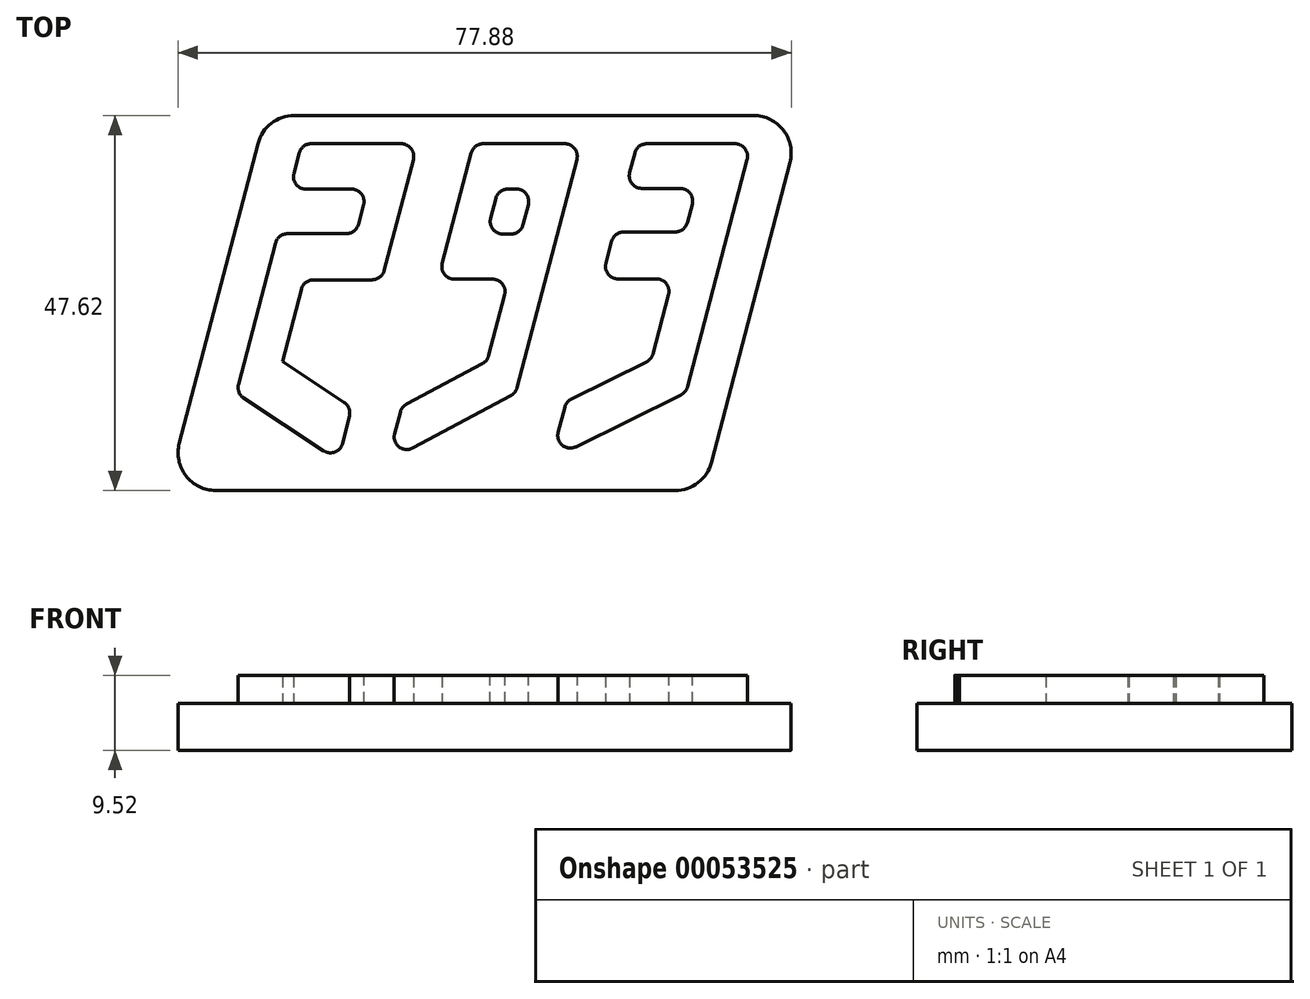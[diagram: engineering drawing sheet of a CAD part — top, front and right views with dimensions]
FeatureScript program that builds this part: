
annotation { "Feature Type Name" : "Feature", "Feature Type Description" : "" }
export const myFeature = defineFeature(function(context is Context, id is Id, definition is map)
    precondition{}
    {
        {
            var Q0;
            Q0=qCreatedBy(makeId("Top.planeOp"),FACE);
            var sketch = newSketch(context, id + "F0", { "sketchPlane" : qUnion([Q0])});
            skLineSegment(sketch, "E0", {"start": v(0, 0) * mm, "end": v(18.18, 0) * mm});
            skLineSegment(sketch, "E1", {"start": v(0, 0) * mm, "end": v(-6.01, -22.93) * mm});
            skLineSegment(sketch, "E2", {"start": v(-6.01, -22.93) * mm, "end": v(5.94, -22.93) * mm});
            skLineSegment(sketch, "E3", {"start": v(5.94, -22.93) * mm, "end": v(2.3, -36.8) * mm});
            skLineSegment(sketch, "E4", {"start": v(2.3, -36.8) * mm, "end": v(-12.18, -44.54) * mm});
            skLineSegment(sketch, "E5", {"start": v(-12.18, -44.54) * mm, "end": v(-14.61, -53.83) * mm});
            skLineSegment(sketch, "E6", {"start": v(-14.61, -53.83) * mm, "end": v(7.12, -42.22) * mm});
            skLineSegment(sketch, "E7", {"start": v(7.12, -42.22) * mm, "end": v(18.18, 0) * mm});
            skLineSegment(sketch, "E8", {"start": v(4.18, -7.66) * mm, "end": v(9.95, -7.66) * mm});
            skLineSegment(sketch, "E9", {"start": v(9.95, -7.66) * mm, "end": v(7.94, -15.3) * mm});
            skLineSegment(sketch, "E10", {"start": v(7.94, -15.3) * mm, "end": v(2.18, -15.3) * mm});
            skLineSegment(sketch, "E11", {"start": v(2.18, -15.3) * mm, "end": v(4.18, -7.66) * mm});
            skLineSegment(sketch, "E12", {"start": v(27.7, 0) * mm, "end": v(47, 0) * mm});
            skLineSegment(sketch, "E13", {"start": v(47, 0) * mm, "end": v(35.97, -42.12) * mm});
            skLineSegment(sketch, "E14", {"start": v(35.97, -42.12) * mm, "end": v(13.14, -53.38) * mm});
            skLineSegment(sketch, "E15", {"start": v(13.14, -53.38) * mm, "end": v(15.68, -43.68) * mm});
            skLineSegment(sketch, "E16", {"start": v(15.68, -43.68) * mm, "end": v(30.12, -36.55) * mm});
            skLineSegment(sketch, "E17", {"start": v(30.12, -36.55) * mm, "end": v(33.7, -22.9) * mm});
            skLineSegment(sketch, "E18", {"start": v(33.7, -22.9) * mm, "end": v(21.7, -22.9) * mm});
            skLineSegment(sketch, "E19", {"start": v(21.7, -22.9) * mm, "end": v(23.8, -14.93) * mm});
            skLineSegment(sketch, "E20", {"start": v(23.8, -14.93) * mm, "end": v(35.78, -14.93) * mm});
            skLineSegment(sketch, "E21", {"start": v(35.78, -14.93) * mm, "end": v(37.72, -7.56) * mm});
            skLineSegment(sketch, "E22", {"start": v(37.72, -7.56) * mm, "end": v(25.73, -7.56) * mm});
            skLineSegment(sketch, "E23", {"start": v(25.73, -7.56) * mm, "end": v(27.7, 0) * mm});
            skLineSegment(sketch, "E24", {"start": v(-29.14, 0) * mm, "end": v(-9.52, 0) * mm});
            skLineSegment(sketch, "E25", {"start": v(-9.52, 0) * mm, "end": v(-15.56, -23.05) * mm});
            skLineSegment(sketch, "E26", {"start": v(-29.14, 0) * mm, "end": v(-31.15, -7.69) * mm});
            skLineSegment(sketch, "E27", {"start": v(-31.15, -7.69) * mm, "end": v(-17.95, -7.69) * mm});
            skLineSegment(sketch, "E28", {"start": v(-17.95, -7.69) * mm, "end": v(-19.92, -15.23) * mm});
            skLineSegment(sketch, "E29", {"start": v(-19.92, -15.23) * mm, "end": v(-33.13, -15.23) * mm});
            skLineSegment(sketch, "E30", {"start": v(-15.56, -23.05) * mm, "end": v(-28.77, -23.05) * mm});
            skLineSegment(sketch, "E31", {"start": v(-28.77, -23.05) * mm, "end": v(-32.4, -36.9) * mm});
            skLineSegment(sketch, "E32", {"start": v(-32.4, -36.9) * mm, "end": v(-20.7, -44.63) * mm});
            skLineSegment(sketch, "E33", {"start": v(-20.7, -44.63) * mm, "end": v(-22.88, -53.67) * mm});
            skLineSegment(sketch, "E34", {"start": v(-22.88, -53.67) * mm, "end": v(-40.2, -42.23) * mm});
            skLineSegment(sketch, "E35", {"start": v(-40.2, -42.23) * mm, "end": v(-33.13, -15.23) * mm});
            skLineSegment(sketch, "E36", {"start": v(-36.54, 0.04) * mm, "end": v(-49.85, -50.76) * mm});
            skLineSegment(sketch, "E37", {"start": v(-43.7, -58.72) * mm, "end": v(34.12, -58.72) * mm});
            skLineSegment(sketch, "E38", {"start": v(40.26, -53.98) * mm, "end": v(53.58, -3.18) * mm});
            skLineSegment(sketch, "E39", {"start": v(-30.4, 4.78) * mm, "end": v(47.43, 4.78) * mm});
            skPoint(sketch, "E40.visualSharp", {"position": v(-35.3, 4.78) * mm});
            skArc(sketch, "E40.filletArc", {"start": v(-30.4, 4.78) * mm, "mid": v(-34.27, 3.45) * mm, "end": v(-36.54, 0.04) * mm});
            skPoint(sketch, "E41.visualSharp", {"position": v(-51.94, -58.72) * mm});
            skArc(sketch, "E41.filletArc", {"start": v(-49.85, -50.76) * mm, "mid": v(-48.73, -56.25) * mm, "end": v(-43.7, -58.72) * mm});
            skPoint(sketch, "E42.visualSharp", {"position": v(39.02, -58.72) * mm});
            skArc(sketch, "E42.filletArc", {"start": v(34.12, -58.72) * mm, "mid": v(38, -57.4) * mm, "end": v(40.26, -53.98) * mm});
            skPoint(sketch, "E43.visualSharp", {"position": v(55.66, 4.78) * mm});
            skArc(sketch, "E43.filletArc", {"start": v(53.58, -3.18) * mm, "mid": v(52.46, 2.3) * mm, "end": v(47.43, 4.78) * mm});
            skSolve(sketch);
        }
        {
            var Q0;
            Q0=makeQuery(id+"F0.imprint","IMPRINT",FACE,{"disambiguationData":[TD([[makeQuery(id+"F0.imprint","IMPRINT",EDGE,{"derivedFrom":sQuery(id+"F0.wireOp",EDGE,"E12")}),-1.0]])]});
            var Q1;
            Q1=makeQuery(id+"F0.imprint","IMPRINT",FACE,{"disambiguationData":[TD([[makeQuery(id+"F0.imprint","IMPRINT",EDGE,{"derivedFrom":sQuery(id+"F0.wireOp",EDGE,"E0")}),-1.0]])]});
            var Q2;
            Q2=makeQuery(id+"F0.imprint","IMPRINT",FACE,{"disambiguationData":[TD([[makeQuery(id+"F0.imprint","IMPRINT",EDGE,{"derivedFrom":sQuery(id+"F0.wireOp",EDGE,"E24")}),-1.0]])]});
            extrude(context, id + "F1", {"entities" : qUnion([Q0, Q1, Q2]), "depth" : 4.76 * mm});
        }
        {
            var Q0;
            Q0=makeQuery(id+"F0.imprint","IMPRINT",FACE,{"disambiguationData":[TD([[makeQuery(id+"F0.imprint","IMPRINT",EDGE,{"derivedFrom":sQuery(id+"F0.wireOp",EDGE,"E0")}),1.0]])]});
            var Q1;
            Q1=makeQuery(id+"F0.imprint","IMPRINT",FACE,{"disambiguationData":[TD([[makeQuery(id+"F0.imprint","IMPRINT",EDGE,{"derivedFrom":sQuery(id+"F0.wireOp",EDGE,"E0")}),-1.0]])]});
            var Q2;
            Q2=makeQuery(id+"F0.imprint","IMPRINT",FACE,{"disambiguationData":[TD([[makeQuery(id+"F0.imprint","IMPRINT",EDGE,{"derivedFrom":sQuery(id+"F0.wireOp",EDGE,"E12")}),-1.0]])]});
            var Q3;
            Q3=makeQuery(id+"F0.imprint","IMPRINT",FACE,{"disambiguationData":[TD([[makeQuery(id+"F0.imprint","IMPRINT",EDGE,{"derivedFrom":sQuery(id+"F0.wireOp",EDGE,"E24")}),-1.0]])]});
            var Q4;
            Q4=makeQuery(id+"F0.imprint","IMPRINT",FACE,{"disambiguationData":[TD([[makeQuery(id+"F0.imprint","IMPRINT",EDGE,{"derivedFrom":sQuery(id+"F0.wireOp",EDGE,"E8")}),-1.0]])]});
            extrude(context, id + "F2", {"entities" : qUnion([Q0, Q1, Q2, Q3, Q4]), "operationType" : NewBodyOperationType.ADD, "oppositeDirection" : true, "depth" : 7.94 * mm});
        }
        {
            var Q0;
            Q0=makeQuery(id+"F1.opExtrude","SWEPT_BODY",BODY,{"disambiguationData":[OSD([sQuery(id+"F0.wireOp",EDGE,"E0"),sQuery(id+"F0.wireOp",EDGE,"E1"),sQuery(id+"F0.wireOp",EDGE,"E2"),sQuery(id+"F0.wireOp",EDGE,"E3"),sQuery(id+"F0.wireOp",EDGE,"E4"),sQuery(id+"F0.wireOp",EDGE,"E5"),sQuery(id+"F0.wireOp",EDGE,"E6"),sQuery(id+"F0.wireOp",EDGE,"E7"),sQuery(id+"F0.wireOp",EDGE,"E8"),sQuery(id+"F0.wireOp",EDGE,"E9"),sQuery(id+"F0.wireOp",EDGE,"E10"),sQuery(id+"F0.wireOp",EDGE,"E11")])]});
            var Q1;
            Q1=qCreatedBy(makeId("Origin.pointOp"),VERTEX);
            transform(context, id + "F3", {"entities" : qUnion([Q0]), "transformType" : TransformType.SCALE_UNIFORMLY, "scale" : .75, "makeCopy" : false, "scalePoint" : qUnion([Q1])});
        }
        {
            var Q0;
            Q0=makeQuery(id+"F1.opExtrude","SWEPT_EDGE",EDGE,{"disambiguationData":[OSD([sQuery(id+"F0.wireOp",EDGE,"E24"),sQuery(id+"F0.wireOp",EDGE,"E26")])]});
            var Q1;
            Q1=makeQuery(id+"F1.opExtrude","SWEPT_EDGE",EDGE,{"disambiguationData":[OSD([sQuery(id+"F0.wireOp",EDGE,"E26"),sQuery(id+"F0.wireOp",EDGE,"E27")])]});
            var Q2;
            Q2=makeQuery(id+"F1.opExtrude","SWEPT_EDGE",EDGE,{"disambiguationData":[OSD([sQuery(id+"F0.wireOp",EDGE,"E27"),sQuery(id+"F0.wireOp",EDGE,"E28")])]});
            var Q3;
            Q3=makeQuery(id+"F1.opExtrude","SWEPT_EDGE",EDGE,{"disambiguationData":[OSD([sQuery(id+"F0.wireOp",EDGE,"E28"),sQuery(id+"F0.wireOp",EDGE,"E29")])]});
            var Q4;
            Q4=makeQuery(id+"F1.opExtrude","SWEPT_EDGE",EDGE,{"disambiguationData":[OSD([sQuery(id+"F0.wireOp",EDGE,"E35"),sQuery(id+"F0.wireOp",EDGE,"E29")])]});
            var Q5;
            Q5=makeQuery(id+"F1.opExtrude","SWEPT_EDGE",EDGE,{"disambiguationData":[OSD([sQuery(id+"F0.wireOp",EDGE,"E34"),sQuery(id+"F0.wireOp",EDGE,"E35")])]});
            var Q6;
            Q6=makeQuery(id+"F1.opExtrude","SWEPT_EDGE",EDGE,{"disambiguationData":[OSD([sQuery(id+"F0.wireOp",EDGE,"E33"),sQuery(id+"F0.wireOp",EDGE,"E34")])]});
            var Q7;
            Q7=makeQuery(id+"F1.opExtrude","SWEPT_EDGE",EDGE,{"disambiguationData":[OSD([sQuery(id+"F0.wireOp",EDGE,"E32"),sQuery(id+"F0.wireOp",EDGE,"E33")])]});
            var Q8;
            Q8=makeQuery(id+"F1.opExtrude","SWEPT_EDGE",EDGE,{"disambiguationData":[OSD([sQuery(id+"F0.wireOp",EDGE,"E30"),sQuery(id+"F0.wireOp",EDGE,"E31")])]});
            var Q9;
            Q9=makeQuery(id+"F1.opExtrude","SWEPT_EDGE",EDGE,{"disambiguationData":[OSD([sQuery(id+"F0.wireOp",EDGE,"E25"),sQuery(id+"F0.wireOp",EDGE,"E30")])]});
            var Q10;
            Q10=makeQuery(id+"F1.opExtrude","SWEPT_EDGE",EDGE,{"disambiguationData":[OSD([sQuery(id+"F0.wireOp",EDGE,"E1"),sQuery(id+"F0.wireOp",EDGE,"E2")])]});
            var Q11;
            Q11=makeQuery(id+"F1.opExtrude","SWEPT_EDGE",EDGE,{"disambiguationData":[OSD([sQuery(id+"F0.wireOp",EDGE,"E2"),sQuery(id+"F0.wireOp",EDGE,"E3")])]});
            var Q12;
            Q12=makeQuery(id+"F1.opExtrude","SWEPT_EDGE",EDGE,{"disambiguationData":[OSD([sQuery(id+"F0.wireOp",EDGE,"E3"),sQuery(id+"F0.wireOp",EDGE,"E4")])]});
            var Q13;
            Q13=makeQuery(id+"F1.opExtrude","SWEPT_EDGE",EDGE,{"disambiguationData":[OSD([sQuery(id+"F0.wireOp",EDGE,"E4"),sQuery(id+"F0.wireOp",EDGE,"E5")])]});
            var Q14;
            Q14=makeQuery(id+"F1.opExtrude","SWEPT_EDGE",EDGE,{"disambiguationData":[OSD([sQuery(id+"F0.wireOp",EDGE,"E5"),sQuery(id+"F0.wireOp",EDGE,"E6")])]});
            var Q15;
            Q15=makeQuery(id+"F1.opExtrude","SWEPT_EDGE",EDGE,{"disambiguationData":[OSD([sQuery(id+"F0.wireOp",EDGE,"E6"),sQuery(id+"F0.wireOp",EDGE,"E7")])]});
            var Q16;
            Q16=makeQuery(id+"F1.opExtrude","SWEPT_EDGE",EDGE,{"disambiguationData":[OSD([sQuery(id+"F0.wireOp",EDGE,"E0"),sQuery(id+"F0.wireOp",EDGE,"E7")])]});
            var Q17;
            Q17=makeQuery(id+"F1.opExtrude","SWEPT_EDGE",EDGE,{"disambiguationData":[OSD([sQuery(id+"F0.wireOp",EDGE,"E0"),sQuery(id+"F0.wireOp",EDGE,"E1")])]});
            var Q18;
            Q18=makeQuery(id+"F1.opExtrude","SWEPT_EDGE",EDGE,{"disambiguationData":[OSD([sQuery(id+"F0.wireOp",EDGE,"E8"),sQuery(id+"F0.wireOp",EDGE,"E11")])]});
            var Q19;
            Q19=makeQuery(id+"F1.opExtrude","SWEPT_EDGE",EDGE,{"disambiguationData":[OSD([sQuery(id+"F0.wireOp",EDGE,"E10"),sQuery(id+"F0.wireOp",EDGE,"E11")])]});
            var Q20;
            Q20=makeQuery(id+"F1.opExtrude","SWEPT_EDGE",EDGE,{"disambiguationData":[OSD([sQuery(id+"F0.wireOp",EDGE,"E8"),sQuery(id+"F0.wireOp",EDGE,"E9")])]});
            var Q21;
            Q21=makeQuery(id+"F1.opExtrude","SWEPT_EDGE",EDGE,{"disambiguationData":[OSD([sQuery(id+"F0.wireOp",EDGE,"E9"),sQuery(id+"F0.wireOp",EDGE,"E10")])]});
            var Q22;
            Q22=makeQuery(id+"F1.opExtrude","SWEPT_EDGE",EDGE,{"disambiguationData":[OSD([sQuery(id+"F0.wireOp",EDGE,"E24"),sQuery(id+"F0.wireOp",EDGE,"E25")])]});
            fillet(context, id + "F4", {"entities" : qUnion([Q0, Q1, Q2, Q3, Q4, Q5, Q6, Q7, Q8, Q9, Q10, Q11, Q12, Q13, Q14, Q15, Q16, Q17, Q18, Q19, Q20, Q21, Q22]), "radius" : 1.59 * mm, "tangentPropagation" : true, "allowEdgeOverflow" : false});
        }
        {
            var Q0;
            Q0=makeQuery(id+"F1.opExtrude","SWEPT_EDGE",EDGE,{"disambiguationData":[OSD([sQuery(id+"F0.wireOp",EDGE,"E21"),sQuery(id+"F0.wireOp",EDGE,"E22")])]});
            var Q1;
            Q1=makeQuery(id+"F1.opExtrude","SWEPT_EDGE",EDGE,{"disambiguationData":[OSD([sQuery(id+"F0.wireOp",EDGE,"E22"),sQuery(id+"F0.wireOp",EDGE,"E23")])]});
            var Q2;
            Q2=makeQuery(id+"F1.opExtrude","SWEPT_EDGE",EDGE,{"disambiguationData":[OSD([sQuery(id+"F0.wireOp",EDGE,"E12"),sQuery(id+"F0.wireOp",EDGE,"E23")])]});
            var Q3;
            Q3=makeQuery(id+"F1.opExtrude","SWEPT_EDGE",EDGE,{"disambiguationData":[OSD([sQuery(id+"F0.wireOp",EDGE,"E19"),sQuery(id+"F0.wireOp",EDGE,"E20")])]});
            var Q4;
            Q4=makeQuery(id+"F1.opExtrude","SWEPT_EDGE",EDGE,{"disambiguationData":[OSD([sQuery(id+"F0.wireOp",EDGE,"E18"),sQuery(id+"F0.wireOp",EDGE,"E19")])]});
            var Q5;
            Q5=makeQuery(id+"F1.opExtrude","SWEPT_EDGE",EDGE,{"disambiguationData":[OSD([sQuery(id+"F0.wireOp",EDGE,"E17"),sQuery(id+"F0.wireOp",EDGE,"E18")])]});
            var Q6;
            Q6=makeQuery(id+"F1.opExtrude","SWEPT_EDGE",EDGE,{"disambiguationData":[OSD([sQuery(id+"F0.wireOp",EDGE,"E15"),sQuery(id+"F0.wireOp",EDGE,"E16")])]});
            var Q7;
            Q7=makeQuery(id+"F1.opExtrude","SWEPT_EDGE",EDGE,{"disambiguationData":[OSD([sQuery(id+"F0.wireOp",EDGE,"E14"),sQuery(id+"F0.wireOp",EDGE,"E15")])]});
            var Q8;
            Q8=makeQuery(id+"F1.opExtrude","SWEPT_EDGE",EDGE,{"disambiguationData":[OSD([sQuery(id+"F0.wireOp",EDGE,"E13"),sQuery(id+"F0.wireOp",EDGE,"E14")])]});
            var Q9;
            Q9=makeQuery(id+"F1.opExtrude","SWEPT_EDGE",EDGE,{"disambiguationData":[OSD([sQuery(id+"F0.wireOp",EDGE,"E16"),sQuery(id+"F0.wireOp",EDGE,"E17")])]});
            var Q10;
            Q10=makeQuery(id+"F1.opExtrude","SWEPT_EDGE",EDGE,{"disambiguationData":[OSD([sQuery(id+"F0.wireOp",EDGE,"E20"),sQuery(id+"F0.wireOp",EDGE,"E21")])]});
            var Q11;
            Q11=makeQuery(id+"F1.opExtrude","SWEPT_EDGE",EDGE,{"disambiguationData":[OSD([sQuery(id+"F0.wireOp",EDGE,"E12"),sQuery(id+"F0.wireOp",EDGE,"E13")])]});
            fillet(context, id + "F5", {"entities" : qUnion([Q0, Q1, Q2, Q3, Q4, Q5, Q6, Q7, Q8, Q9, Q10, Q11]), "radius" : 1.59 * mm, "tangentPropagation" : true, "allowEdgeOverflow" : false});
        }
    });
